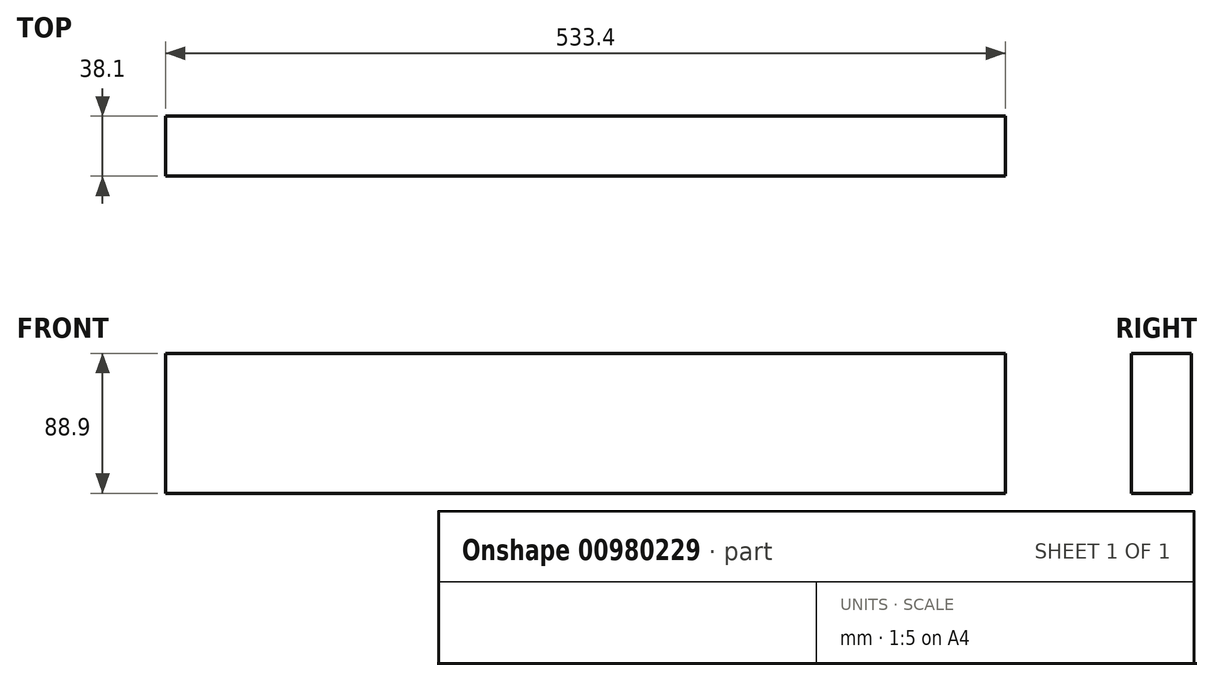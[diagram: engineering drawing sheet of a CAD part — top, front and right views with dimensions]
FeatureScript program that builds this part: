
annotation { "Feature Type Name" : "Feature", "Feature Type Description" : "" }
export const myFeature = defineFeature(function(context is Context, id is Id, definition is map)
    precondition{}
    {
        {
            var Q0;
            Q0=qCreatedBy(makeId("Right.planeOp"),FACE);
            var sketch = newSketch(context, id + "F0", { "sketchPlane" : qUnion([Q0])});
            skLineSegment(sketch, "E0.bottom", {"start": v(-19.05, -44.45) * mm, "end": v(19.05, -44.45) * mm});
            skLineSegment(sketch, "E0.top", {"start": v(-19.05, 44.45) * mm, "end": v(19.05, 44.45) * mm});
            skLineSegment(sketch, "E0.left", {"start": v(-19.05, -44.45) * mm, "end": v(-19.05, 44.45) * mm});
            skLineSegment(sketch, "E0.right", {"start": v(19.05, -44.45) * mm, "end": v(19.05, 44.45) * mm});
            skPoint(sketch, "E0.middle", {"position": v(0, 0) * mm});
            skSolve(sketch);
        }
        {
            var Q0;
            Q0=makeQuery(id+"F0.imprint","IMPRINT",FACE,{"disambiguationData":[TD([[makeQuery(id+"F0.imprint","IMPRINT",EDGE,{"derivedFrom":sQuery(id+"F0.wireOp",EDGE,"E0.bottom")}),1.0]])]});
            extrude(context, id + "F1", {"entities" : qUnion([Q0]), "oppositeDirection" : true, "depth" : 533.4 * mm, "offsetDistance" : 25.4 * mm});
        }
    });
